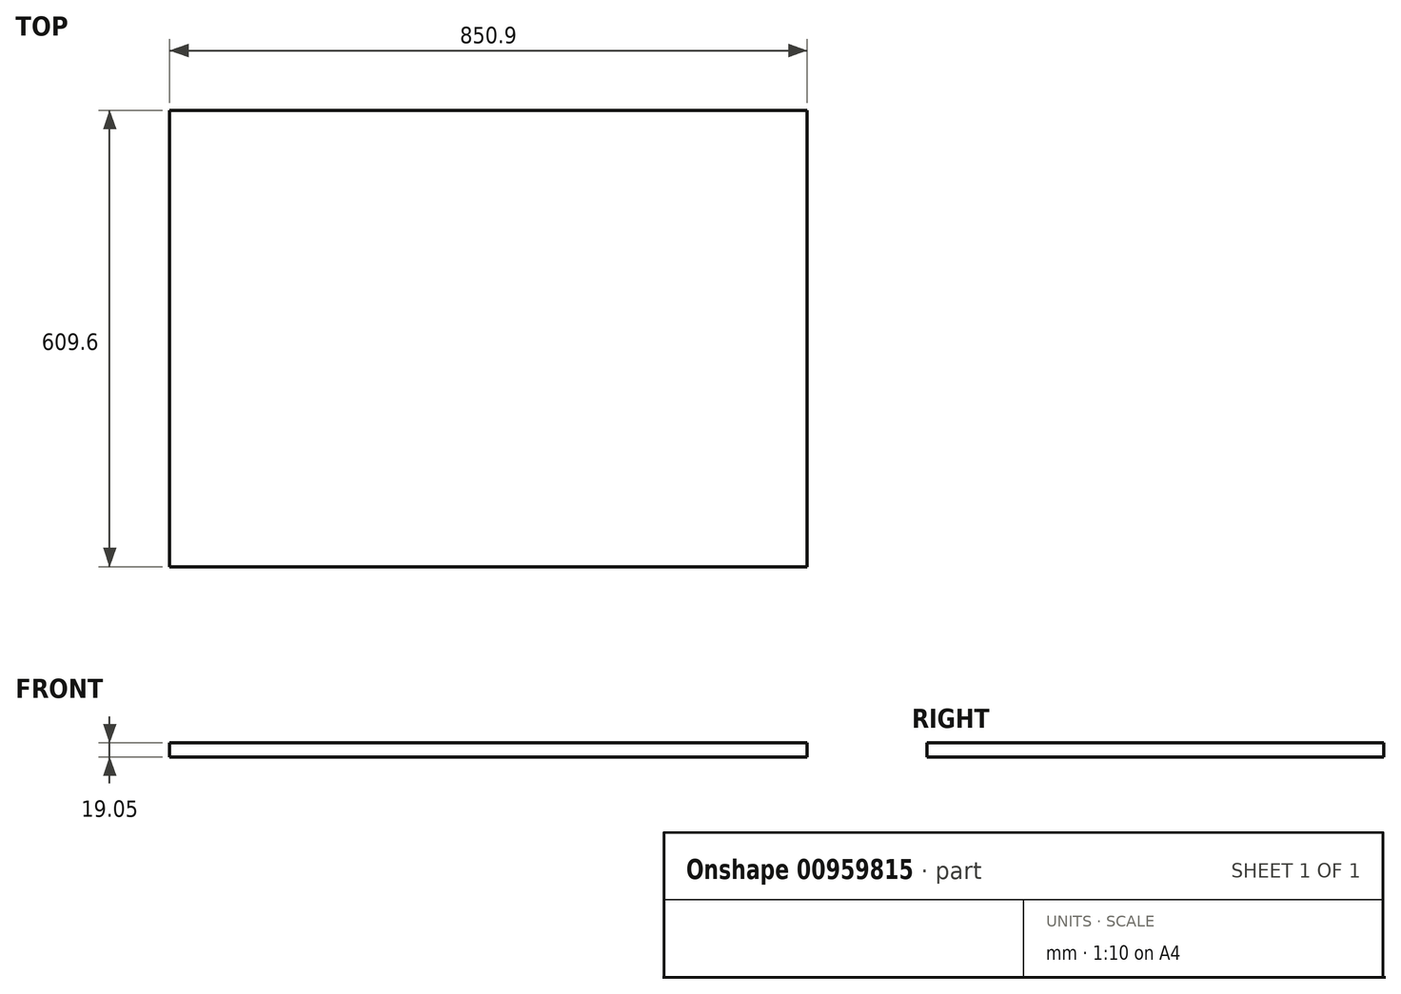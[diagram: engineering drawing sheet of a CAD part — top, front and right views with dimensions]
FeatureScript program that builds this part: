
annotation { "Feature Type Name" : "Feature", "Feature Type Description" : "" }
export const myFeature = defineFeature(function(context is Context, id is Id, definition is map)
    precondition{}
    {
        {
            var Q0;
            Q0=qCreatedBy(makeId("Top.planeOp"),FACE);
            var sketch = newSketch(context, id + "F0", { "sketchPlane" : qUnion([Q0])});
            skLineSegment(sketch, "E0.bottom", {"start": v(425.45, 304.8) * mm, "end": v(-425.45, 304.8) * mm});
            skLineSegment(sketch, "E0.top", {"start": v(425.45, -304.8) * mm, "end": v(-425.45, -304.8) * mm});
            skLineSegment(sketch, "E0.left", {"start": v(425.45, 304.8) * mm, "end": v(425.45, -304.8) * mm});
            skLineSegment(sketch, "E0.right", {"start": v(-425.45, 304.8) * mm, "end": v(-425.45, -304.8) * mm});
            skPoint(sketch, "E0.middle", {"position": v(0, 0) * mm});
            skSolve(sketch);
        }
        {
            var Q0;
            Q0=makeQuery(id+"F0.imprint","IMPRINT",FACE,{"disambiguationData":[TD([[makeQuery(id+"F0.imprint","IMPRINT",EDGE,{"derivedFrom":sQuery(id+"F0.wireOp",EDGE,"E0.bottom")}),1.0]])]});
            extrude(context, id + "F1", {"entities" : qUnion([Q0]), "depth" : 19.05 * mm, "offsetDistance" : 25.4 * mm});
        }
    });
